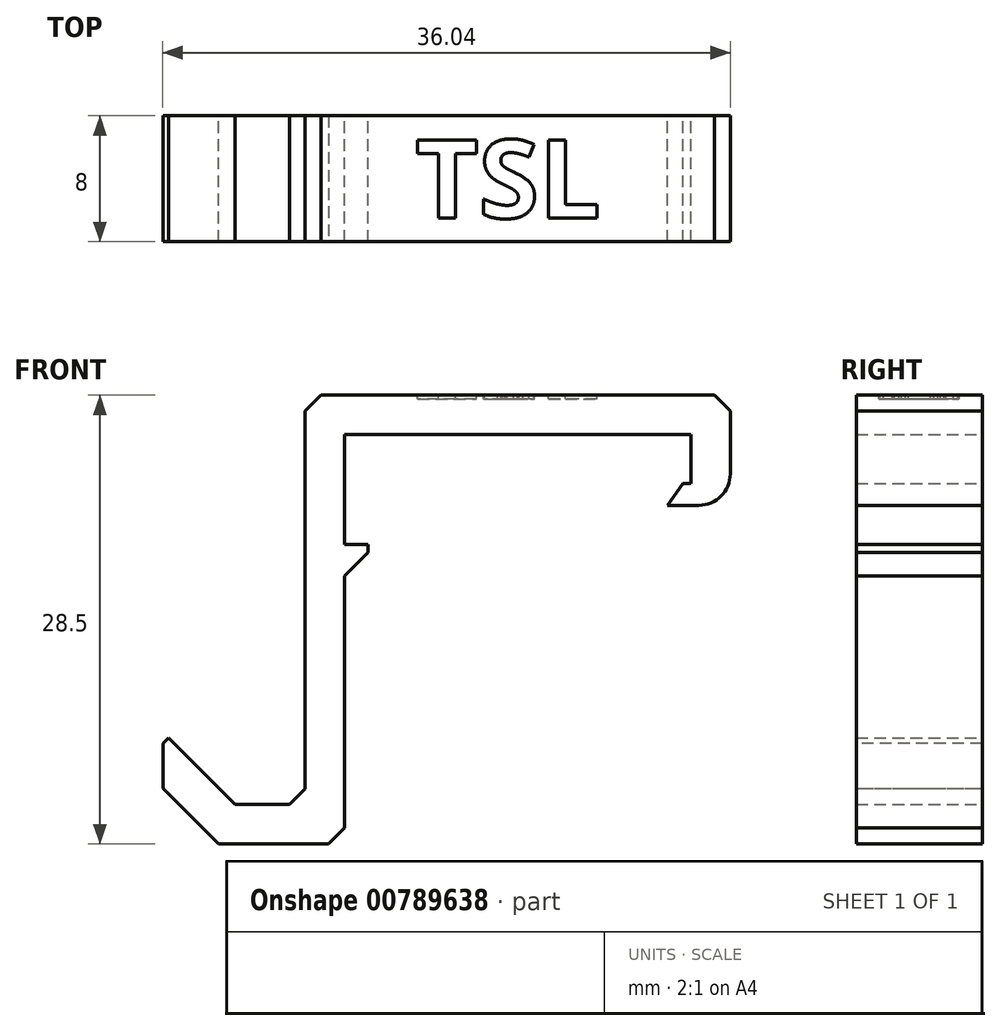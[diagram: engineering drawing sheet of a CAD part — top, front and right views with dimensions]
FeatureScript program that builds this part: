
annotation { "Feature Type Name" : "Feature", "Feature Type Description" : "" }
export const myFeature = defineFeature(function(context is Context, id is Id, definition is map)
    precondition{}
    {
        {
            var Q0;
            Q0=qCreatedBy(makeId("Front.planeOp"),FACE);
            var sketch = newSketch(context, id + "F0", { "sketchPlane" : qUnion([Q0])});
            skLineSegment(sketch, "E0.bottom", {"start": v(0, 0) * mm, "end": v(50, 0) * mm, "construction": true});
            skLineSegment(sketch, "E0.top", {"start": v(0, 25) * mm, "end": v(50, 25) * mm, "construction": true});
            skLineSegment(sketch, "E0.left", {"start": v(0, 0) * mm, "end": v(0, 25) * mm, "construction": true});
            skLineSegment(sketch, "E0.right", {"start": v(50, 0) * mm, "end": v(50, 25) * mm, "construction": true});
            skLineSegment(sketch, "E1.0", {"start": v(50.5, -0.5) * mm, "end": v(50.5, 25.5) * mm, "construction": true});
            skLineSegment(sketch, "E1.1", {"start": v(-0.5, -0.5) * mm, "end": v(50.5, -0.5) * mm, "construction": true});
            skLineSegment(sketch, "E1.2", {"start": v(-0.5, -0.5) * mm, "end": v(-0.5, 16) * mm, "construction": true});
            skLineSegment(sketch, "E1.3", {"start": v(-0.5, 25.5) * mm, "end": v(50.5, 25.5) * mm, "construction": true});
            skLineSegment(sketch, "E2.0", {"start": v(2.6, 22.4) * mm, "end": v(18, 22.4) * mm, "construction": true});
            skLineSegment(sketch, "E2.1", {"start": v(2.6, 2.6) * mm, "end": v(2.6, 22.4) * mm, "construction": true});
            skLineSegment(sketch, "E2.2", {"start": v(2.6, 2.6) * mm, "end": v(45.4, 2.6) * mm, "construction": true});
            skLineSegment(sketch, "E2.3", {"start": v(45.4, 2.6) * mm, "end": v(45.4, 22.4) * mm, "construction": true});
            skLineSegment(sketch, "E3.0", {"start": v(21, 0) * mm, "end": v(21, 25) * mm, "construction": true});
            skLineSegment(sketch, "E4.0", {"start": v(29, 0) * mm, "end": v(29, 25) * mm, "construction": true});
            skLineSegment(sketch, "E5", {"start": v(-0.5, 25.5) * mm, "end": v(-0.5, 18.5) * mm});
            skLineSegment(sketch, "E6", {"start": v(-8.5, -0.5) * mm, "end": v(-13.45, 4.45) * mm});
            skLineSegment(sketch, "E7", {"start": v(-8.5, -0.5) * mm, "end": v(-0.5, -0.5) * mm});
            skLineSegment(sketch, "E8.0", {"start": v(-7.46, 2) * mm, "end": v(-11.68, 6.22) * mm});
            skLineSegment(sketch, "E8.1", {"start": v(-7.46, 2) * mm, "end": v(-3, 2) * mm});
            skLineSegment(sketch, "E8.2", {"start": v(-3, 2) * mm, "end": v(-3, 25.5) * mm});
            skLineSegment(sketch, "E9", {"start": v(-13.45, 4.45) * mm, "end": v(-11.68, 6.22) * mm});
            skLineSegment(sketch, "E10", {"start": v(-0.5, 25.5) * mm, "end": v(21.5, 25.5) * mm});
            skLineSegment(sketch, "E11.0", {"start": v(-0.5, 28) * mm, "end": v(21.5, 28) * mm});
            skLineSegment(sketch, "E12", {"start": v(-0.5, 28) * mm, "end": v(-3, 28) * mm});
            skLineSegment(sketch, "E13", {"start": v(-3, 28) * mm, "end": v(-3, 25.5) * mm});
            skLineSegment(sketch, "E14.bottom", {"start": v(21.5, 28) * mm, "end": v(24, 28) * mm});
            skLineSegment(sketch, "E14.left", {"start": v(21.5, 25.5) * mm, "end": v(21.5, 22.4) * mm});
            skLineSegment(sketch, "E14.right", {"start": v(24, 28) * mm, "end": v(24, 22.4) * mm});
            skLineSegment(sketch, "E15.bottom", {"start": v(21.5, 22.4) * mm, "end": v(21, 22.4) * mm});
            skLineSegment(sketch, "E15.top", {"start": v(24, 21) * mm, "end": v(20, 21) * mm});
            skLineSegment(sketch, "E15.left", {"start": v(24, 22.4) * mm, "end": v(24, 21) * mm});
            skLineSegment(sketch, "E16", {"start": v(13.54, 19) * mm, "end": v(-16.95, 19) * mm, "construction": true});
            skLineSegment(sketch, "E17.bottom", {"start": v(-0.5, 18.5) * mm, "end": v(1, 18.5) * mm});
            skLineSegment(sketch, "E17.top", {"start": v(-0.5, 16) * mm, "end": v(1, 16) * mm});
            skLineSegment(sketch, "E17.right", {"start": v(1, 18.5) * mm, "end": v(1, 16) * mm});
            skLineSegment(sketch, "E18.trimOffspring", {"start": v(24, 22.4) * mm, "end": v(45.4, 22.4) * mm, "construction": true});
            skLineSegment(sketch, "E19.trimOffspring", {"start": v(-0.5, 18.5) * mm, "end": v(-0.5, 25.5) * mm, "construction": true});
            skLineSegment(sketch, "E20.trimOffspring", {"start": v(-0.5, 16) * mm, "end": v(-0.5, -0.5) * mm});
            skLineSegment(sketch, "E21", {"start": v(21, 22.4) * mm, "end": v(20, 21) * mm});
            skLineSegment(sketch, "E22.trimOffspring", {"start": v(21, 22.4) * mm, "end": v(21.5, 22.4) * mm, "construction": true});
            skSolve(sketch);
        }
        {
            var Q0;
            Q0=makeQuery(id+"F0.imprint","IMPRINT",FACE,{"disambiguationData":[TD([[makeQuery(id+"F0.imprint","IMPRINT",EDGE,{"derivedFrom":sQuery(id+"F0.wireOp",EDGE,"E5")}),-1.0]])]});
            extrude(context, id + "F1", {"entities" : qUnion([Q0]), "depth" : 8 * mm, "offsetDistance" : 25 * mm});
        }
        {
            var Q0;
            Q0=makeQuery(id+"F1.opExtrude","SWEPT_EDGE",EDGE,{"disambiguationData":[OSD([sQuery(id+"F0.wireOp",EDGE,"E17.top"),sQuery(id+"F0.wireOp",EDGE,"E17.right")])]});
            var Q1;
            Q1=makeQuery(id+"F1.opExtrude","SWEPT_EDGE",EDGE,{"disambiguationData":[OSD([sQuery(id+"F0.wireOp",EDGE,"E6"),sQuery(id+"F0.wireOp",EDGE,"E9")])]});
            chamfer(context, id + "F2", {"entities" : qUnion([Q0, Q1]), "width" : 2 * mm, "tangentPropagation" : true});
        }
        {
            var Q0;
            {var subQ0=sQuery(id+"F0.wireOp",EDGE,"E15.top");Q0=makeQuery(id+"F2.opChamfer","BLEND_EDGE",EDGE,{"blendedFrom":[makeQuery(id+"F1.opExtrude","SWEPT_EDGE",EDGE,{"disambiguationData":[OSD([subQ0,sQuery(id+"F0.wireOp",EDGE,"E15.right")])]}),makeQuery(id+"F1.opExtrude","SWEPT_FACE",FACE,{"disambiguationData":[OSD([subQ0])]})],"blendedInto":[makeQuery(id+"F1.opExtrude","SWEPT_FACE",FACE,{"disambiguationData":[OSD([subQ0])]})]});}
            var Q1;
            Q1=makeQuery(id+"F1.opExtrude","SWEPT_EDGE",EDGE,{"disambiguationData":[OSD([sQuery(id+"F0.wireOp",EDGE,"E15.top"),sQuery(id+"F0.wireOp",EDGE,"E15.left")])]});
            fillet(context, id + "F3", {"entities" : qUnion([Q0, Q1]), "radius" : 2 * mm, "tangentPropagation" : true, "allowEdgeOverflow" : false});
        }
        {
            var Q0;
            Q0=makeQuery(id+"F1.opExtrude","SWEPT_EDGE",EDGE,{"disambiguationData":[OSD([sQuery(id+"F0.wireOp",EDGE,"E7"),sQuery(id+"F0.wireOp",EDGE,"E20.trimOffspring")])]});
            var Q1;
            Q1=makeQuery(id+"F1.opExtrude","SWEPT_EDGE",EDGE,{"disambiguationData":[OSD([sQuery(id+"F0.wireOp",EDGE,"E8.1"),sQuery(id+"F0.wireOp",EDGE,"E8.2")])]});
            var Q2;
            Q2=makeQuery(id+"F1.opExtrude","SWEPT_EDGE",EDGE,{"disambiguationData":[OSD([sQuery(id+"F0.wireOp",EDGE,"E14.bottom"),sQuery(id+"F0.wireOp",EDGE,"E14.right")])]});
            var Q3;
            Q3=makeQuery(id+"F1.opExtrude","SWEPT_EDGE",EDGE,{"disambiguationData":[OSD([sQuery(id+"F0.wireOp",EDGE,"E12"),sQuery(id+"F0.wireOp",EDGE,"E13")])]});
            chamfer(context, id + "F4", {"entities" : qUnion([Q0, Q1, Q2, Q3]), "width" : 1 * mm, "tangentPropagation" : true});
        }
        {
            var Q0;
            Q0=makeQuery(id+"F1.opExtrude","SWEPT_FACE",FACE,{"disambiguationData":[OSD([sQuery(id+"F0.wireOp",EDGE,"E11.0"),sQuery(id+"F0.wireOp",EDGE,"E12"),sQuery(id+"F0.wireOp",EDGE,"E14.bottom")])]});
            var sketch = newSketch(context, id + "F5", { "sketchPlane" : qUnion([Q0])});
            skText(sketch, "E23", { "text": "TSL", "fontName": "OpenSans-Bold.ttf"});
            const initialGuessF5  = {"E23": [0.004, -0.0065, 1, 0, 0.005]};
            skSetInitialGuess(sketch, initialGuessF5);
            skSolve(sketch);
        }
        {
            var Q0;
            Q0=makeQuery(id+"F5.imprint","IMPRINT",FACE,{"disambiguationData":[TD([[makeQuery(id+"F5.imprint","IMPRINT",EDGE,{"derivedFrom":sQuery(id+"F5.wireOp",EDGE,"E23.sketch_text.stroke-36")}),-1.0]])]});
            var Q1;
            Q1=makeQuery(id+"F5.imprint","IMPRINT",FACE,{"disambiguationData":[TD([[makeQuery(id+"F5.imprint","IMPRINT",EDGE,{"derivedFrom":sQuery(id+"F5.wireOp",EDGE,"E23.sketch_text.stroke-8")}),-1.0]])]});
            var Q2;
            Q2=makeQuery(id+"F5.imprint","IMPRINT",FACE,{"disambiguationData":[TD([[makeQuery(id+"F5.imprint","IMPRINT",EDGE,{"derivedFrom":sQuery(id+"F5.wireOp",EDGE,"E23.sketch_text.stroke-0")}),-1.0]])]});
            extrude(context, id + "F6", {"entities" : qUnion([Q0, Q1, Q2]), "operationType" : NewBodyOperationType.REMOVE, "oppositeDirection" : true, "depth" : 0.25 * mm, "offsetDistance" : 25 * mm});
        }
    });
